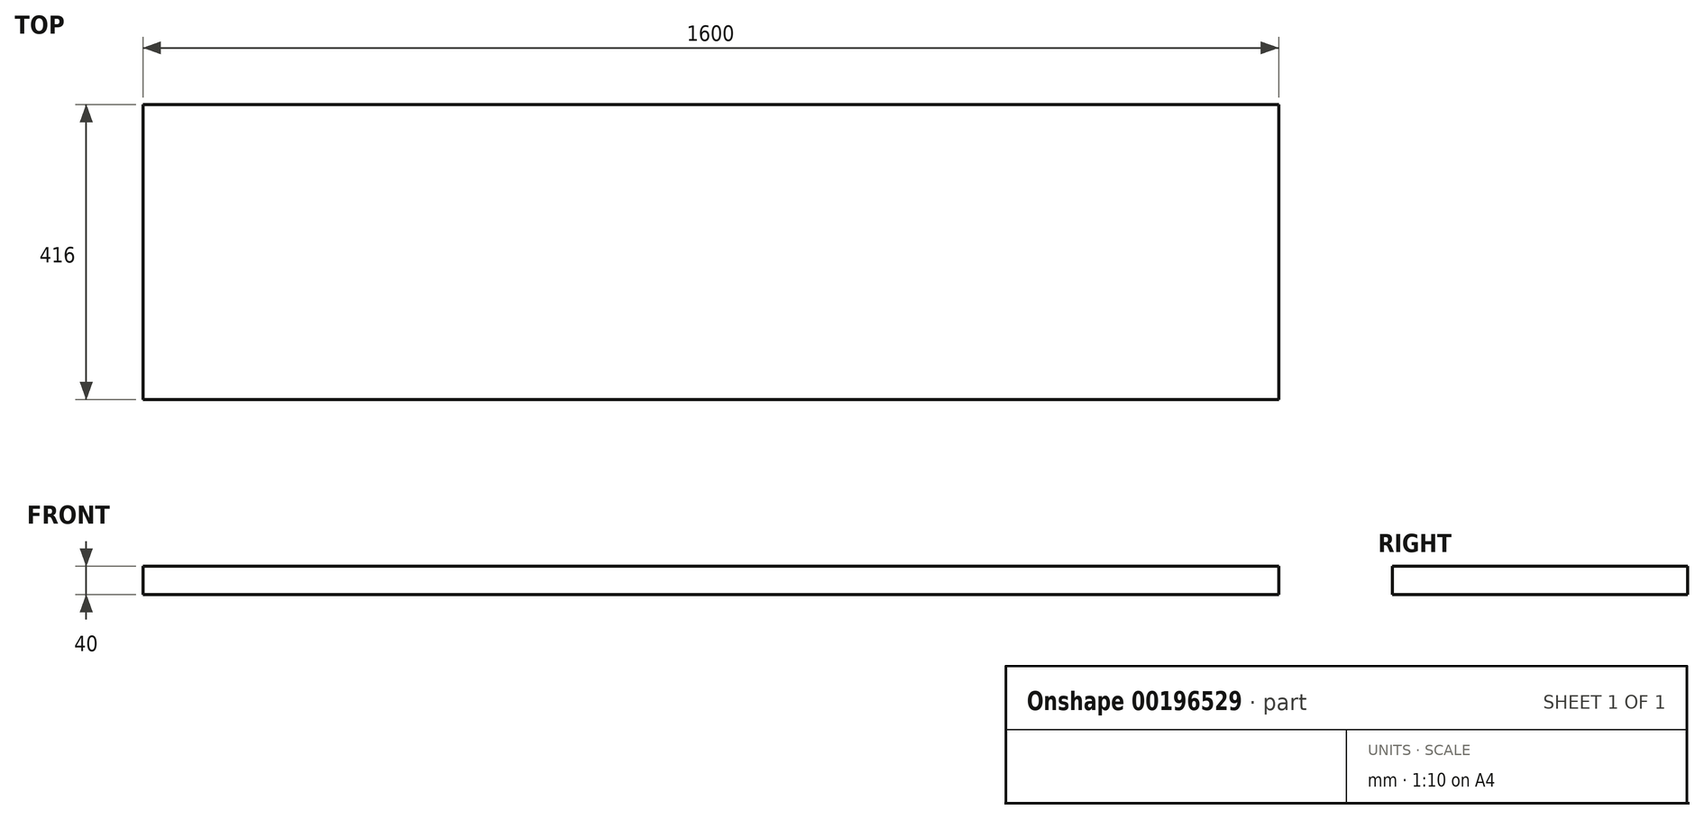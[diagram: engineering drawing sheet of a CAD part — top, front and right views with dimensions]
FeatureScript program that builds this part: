
annotation { "Feature Type Name" : "Feature", "Feature Type Description" : "" }
export const myFeature = defineFeature(function(context is Context, id is Id, definition is map)
    precondition{}
    {
        {
            var Q0;
            Q0=qCreatedBy(makeId("Top.planeOp"),FACE);
            var sketch = newSketch(context, id + "F0", { "sketchPlane" : qUnion([Q0])});
            skLineSegment(sketch, "E0.bottom", {"start": v(-864.34, -235.28) * mm, "end": v(735.66, -235.28) * mm});
            skLineSegment(sketch, "E0.top", {"start": v(-864.34, 180.72) * mm, "end": v(735.66, 180.72) * mm});
            skLineSegment(sketch, "E0.left", {"start": v(-864.34, -235.28) * mm, "end": v(-864.34, 180.72) * mm});
            skLineSegment(sketch, "E0.right", {"start": v(735.66, -235.28) * mm, "end": v(735.66, 180.72) * mm});
            skSolve(sketch);
        }
        {
            var Q0;
            Q0=makeQuery(id+"F0.imprint","IMPRINT",FACE,{"disambiguationData":[TD([[makeQuery(id+"F0.imprint","IMPRINT",EDGE,{"derivedFrom":sQuery(id+"F0.wireOp",EDGE,"E0.bottom")}),1.0]])]});
            extrude(context, id + "F1", {"entities" : qUnion([Q0]), "depth" : 40 * mm});
        }
    });
